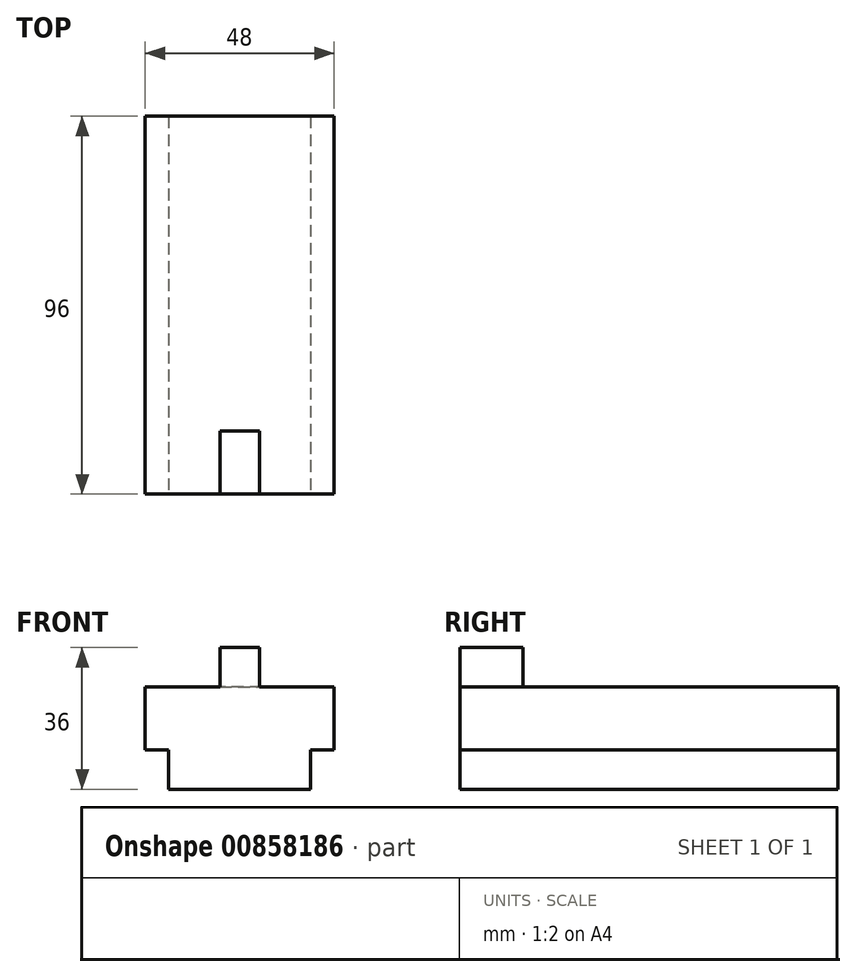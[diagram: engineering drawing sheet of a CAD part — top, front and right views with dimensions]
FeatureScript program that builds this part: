
annotation { "Feature Type Name" : "Feature", "Feature Type Description" : "" }
export const myFeature = defineFeature(function(context is Context, id is Id, definition is map)
    precondition{}
    {
        {
            var Q0;
            Q0=qCreatedBy(makeId("Top.planeOp"),FACE);
            var sketch = newSketch(context, id + "F0", { "sketchPlane" : qUnion([Q0])});
            skLineSegment(sketch, "E0.bottom", {"start": v(18, 48) * mm, "end": v(-18, 48) * mm});
            skLineSegment(sketch, "E0.top", {"start": v(18, -48) * mm, "end": v(-18, -48) * mm});
            skLineSegment(sketch, "E0.left", {"start": v(18, 48) * mm, "end": v(18, -48) * mm});
            skLineSegment(sketch, "E0.right", {"start": v(-18, 48) * mm, "end": v(-18, -48) * mm});
            skPoint(sketch, "E0.middle", {"position": v(0, 0) * mm});
            skSolve(sketch);
        }
        {
            var Q0;
            Q0 = qSketchRegion(id + "F0", true);
            extrude(context, id + "F1", {"entities" : qUnion([Q0]), "depth" : 10 * mm, "offsetDistance" : 25.4 * mm});
        }
        {
            var Q0;
            Q0=makeQuery(id+"F1.opExtrude","CAP_FACE",FACE,{"disambiguationData":[OSD([sQuery(id+"F0.wireOp",EDGE,"E0.bottom"),sQuery(id+"F0.wireOp",EDGE,"E0.top"),sQuery(id+"F0.wireOp",EDGE,"E0.left"),sQuery(id+"F0.wireOp",EDGE,"E0.right")])],"isStart":false});
            var sketch = newSketch(context, id + "F2", { "sketchPlane" : qUnion([Q0])});
            skLineSegment(sketch, "E1.bottom", {"start": v(24, -48) * mm, "end": v(-24, -48) * mm});
            skLineSegment(sketch, "E1.top", {"start": v(24, 48) * mm, "end": v(-24, 48) * mm});
            skLineSegment(sketch, "E1.left", {"start": v(24, -48) * mm, "end": v(24, 48) * mm});
            skLineSegment(sketch, "E1.right", {"start": v(-24, -48) * mm, "end": v(-24, 48) * mm});
            skPoint(sketch, "E1.middle", {"position": v(0, 0) * mm});
            skSolve(sketch);
        }
        {
            var Q0;
            Q0 = qSketchRegion(id + "F2", true);
            extrude(context, id + "F3", {"entities" : qUnion([Q0]), "operationType" : NewBodyOperationType.ADD, "depth" : 16 * mm, "offsetDistance" : 25.4 * mm});
        }
        {
            var Q0;
            Q0=makeQuery(id+"F3.opExtrude","CAP_FACE",FACE,{"disambiguationData":[OSD([sQuery(id+"F2.wireOp",EDGE,"E1.bottom"),sQuery(id+"F2.wireOp",EDGE,"E1.top"),sQuery(id+"F2.wireOp",EDGE,"E1.left"),sQuery(id+"F2.wireOp",EDGE,"E1.right")])],"isStart":false});
            var sketch = newSketch(context, id + "F4", { "sketchPlane" : qUnion([Q0])});
            skLineSegment(sketch, "E2.bottom", {"start": v(-24, -48) * mm, "end": v(24, -48) * mm});
            skLineSegment(sketch, "E2.top", {"start": v(-24, -32) * mm, "end": v(24, -32) * mm});
            skLineSegment(sketch, "E2.left", {"start": v(-24, -48) * mm, "end": v(-24, -32) * mm});
            skLineSegment(sketch, "E2.right", {"start": v(24, -48) * mm, "end": v(24, -32) * mm});
            skSolve(sketch);
        }
        {
            var Q0;
            Q0 = qSketchRegion(id + "F4", true);
            extrude(context, id + "F5", {"entities" : qUnion([Q0]), "operationType" : NewBodyOperationType.ADD, "depth" : 10 * mm, "offsetDistance" : 25.4 * mm});
        }
        {
            var Q0;
            Q0=makeQuery(id+"F5.opExtrude","CAP_FACE",FACE,{"disambiguationData":[OSD([sQuery(id+"F4.wireOp",EDGE,"E2.bottom"),sQuery(id+"F4.wireOp",EDGE,"E2.top"),sQuery(id+"F4.wireOp",EDGE,"E2.left"),sQuery(id+"F4.wireOp",EDGE,"E2.right")])],"isStart":false});
            var sketch = newSketch(context, id + "F6", { "sketchPlane" : qUnion([Q0])});
            skLineSegment(sketch, "E3.bottom", {"start": v(-24, -48) * mm, "end": v(-5, -48) * mm});
            skLineSegment(sketch, "E3.top", {"start": v(-24, -32) * mm, "end": v(-5, -32) * mm});
            skLineSegment(sketch, "E3.left", {"start": v(-24, -48) * mm, "end": v(-24, -32) * mm});
            skLineSegment(sketch, "E3.right", {"start": v(-5, -48) * mm, "end": v(-5, -32) * mm});
            skLineSegment(sketch, "E4.bottom", {"start": v(24, -48) * mm, "end": v(5, -48) * mm});
            skLineSegment(sketch, "E4.top", {"start": v(24, -32) * mm, "end": v(5, -32) * mm});
            skLineSegment(sketch, "E4.left", {"start": v(24, -48) * mm, "end": v(24, -32) * mm});
            skLineSegment(sketch, "E4.right", {"start": v(5, -48) * mm, "end": v(5, -32) * mm});
            skSolve(sketch);
        }
        {
            var Q0;
            Q0 = qSketchRegion(id + "F6", true);
            extrude(context, id + "F7", {"entities" : qUnion([Q0]), "operationType" : NewBodyOperationType.REMOVE, "oppositeDirection" : true, "depth" : 10 * mm, "offsetDistance" : 25.4 * mm});
        }
    });
